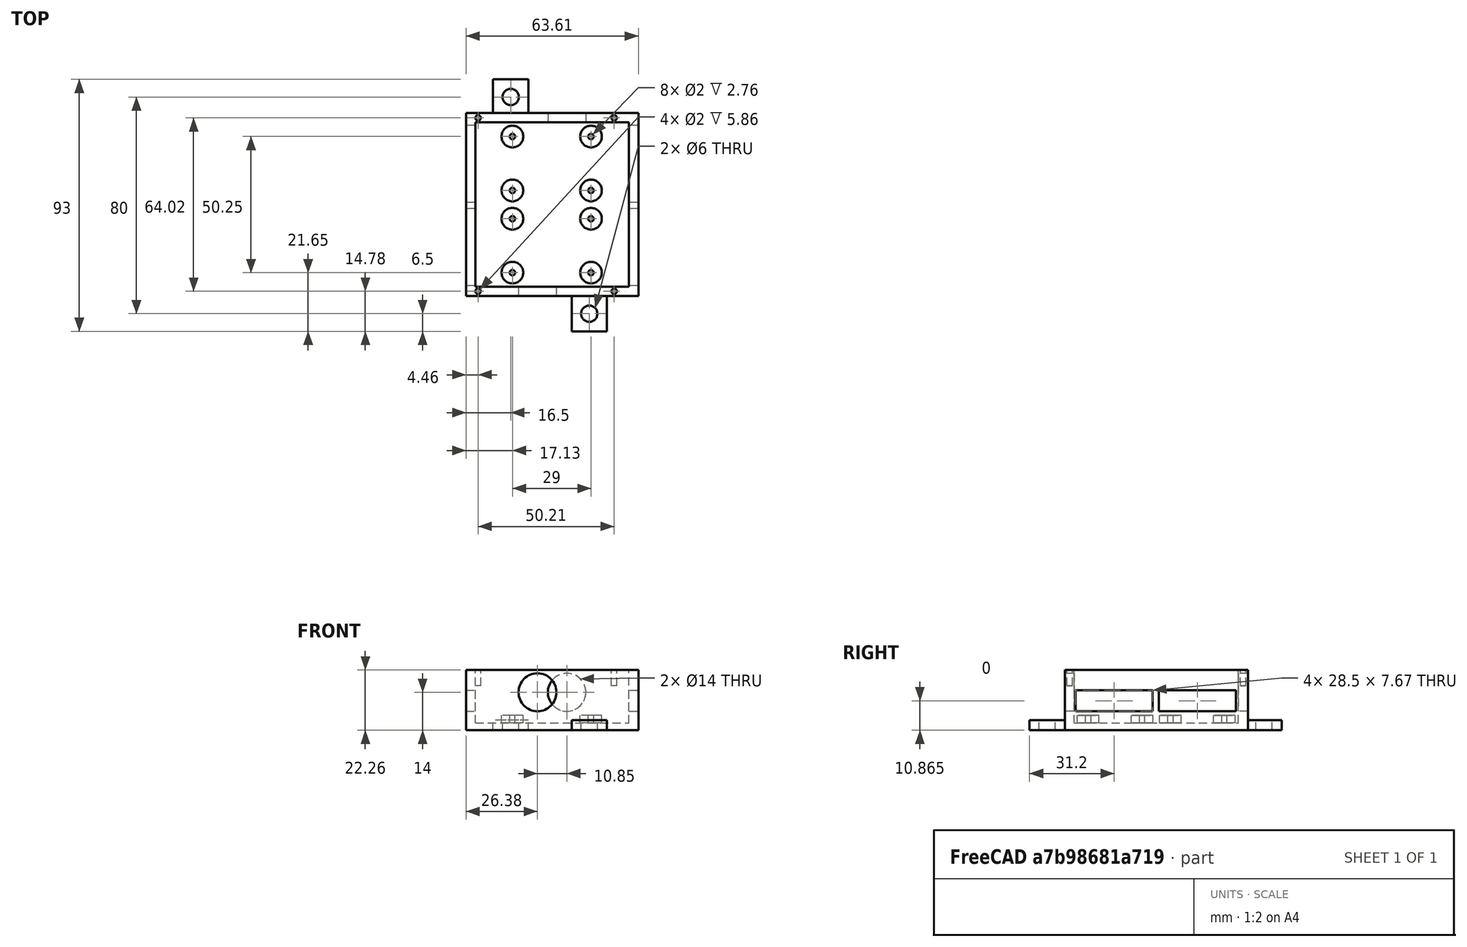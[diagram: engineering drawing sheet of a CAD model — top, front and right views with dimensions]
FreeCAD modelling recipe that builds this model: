
FCSTD DOCUMENT  (FreeCAD 0.15R4671 (Git))
Label: smps_to_dyna_case
License: All rights reserved
LicenseURL: http://en.wikipedia.org/wiki/All_rights_reserved
objects: Part::Cylinder×24, Part::Cut×19, Part::Box×6, Part::MultiFuse×3
note: 52 computed .brp shape members not serialized (recipe doc carries the construction recipe); baked Part::Feature solids carry a one-line shape summary decoded from their .brp

FEATURE [Part::Box] Box  label="Cubo"
  Height = 22.26
  Length = 63.61
  Placement = pos=(0,0,-1) rot=(0,0,1;0rad)
  Width = 67.58
FEATURE [Part::Box] Box001  label="Cubo001"
  Height = 22.6
  Length = 56.67
  Placement = pos=(3.47,3.47,1.67) rot=(0,0,1;0rad)
  Width = 60.64
FEATURE [Part::Cut] Cut
  Base = -> Box
  Tool = -> Box001
FEATURE [Part::Cylinder] Cylinder  label="Cilindro"
  Angle = 360
  Height = 4.43
  Placement = pos=(17.13,8.65,0) rot=(0,0,1;0rad)
  Radius = 1
FEATURE [Part::Cylinder] Cylinder001  label="Cilindro001"
  Angle = 360
  Height = 4.43
  Placement = pos=(17.13,8.65,0) rot=(0,0,1;0rad)
  Radius = 4
FEATURE [Part::Cut] Cut001  label="1"
  Base = -> Cylinder001
  Tool = -> Cylinder
FEATURE [Part::Cylinder] Cylinder002  label="Cilindro002"
  Angle = 360
  Height = 4.43
  Placement = pos=(17.13,8.65,0) rot=(0,0,1;0rad)
  Radius = 1
FEATURE [Part::Cylinder] Cylinder003  label="Cilindro003"
  Angle = 360
  Height = 4.43
  Placement = pos=(17.13,8.65,0) rot=(0,0,1;0rad)
  Radius = 4
FEATURE [Part::Cut] Cut002  label="2"
  Base = -> Cylinder003
  Placement = pos=(29,0,0) rot=(0,0,1;0rad)
  Tool = -> Cylinder002
FEATURE [Part::Cylinder] Cylinder004  label="Cilindro004"
  Angle = 360
  Height = 4.43
  Placement = pos=(17.13,8.65,0) rot=(0,0,1;0rad)
  Radius = 1
FEATURE [Part::Cylinder] Cylinder005  label="Cilindro005"
  Angle = 360
  Height = 4.43
  Placement = pos=(17.13,8.65,0) rot=(0,0,1;0rad)
  Radius = 4
FEATURE [Part::Cut] Cut003  label="3"
  Base = -> Cylinder005
  Placement = pos=(29,19.9,0) rot=(0,0,1;0rad)
  Tool = -> Cylinder004
FEATURE [Part::Cylinder] Cylinder006  label="Cilindro006"
  Angle = 360
  Height = 4.43
  Placement = pos=(17.13,8.65,0) rot=(0,0,1;0rad)
  Radius = 1
FEATURE [Part::Cylinder] Cylinder007  label="Cilindro007"
  Angle = 360
  Height = 4.43
  Placement = pos=(17.13,8.65,0) rot=(0,0,1;0rad)
  Radius = 4
FEATURE [Part::Cut] Cut004  label="8"
  Base = -> Cylinder007
  Placement = pos=(29,30.35,0) rot=(0,0,1;0rad)
  Tool = -> Cylinder006
FEATURE [Part::Cylinder] Cylinder008  label="Cilindro008"
  Angle = 360
  Height = 4.43
  Placement = pos=(17.13,8.65,0) rot=(0,0,1;0rad)
  Radius = 1
FEATURE [Part::Cylinder] Cylinder009  label="Cilindro009"
  Angle = 360
  Height = 4.43
  Placement = pos=(17.13,8.65,0) rot=(0,0,1;0rad)
  Radius = 4
FEATURE [Part::Cut] Cut005  label="7"
  Base = -> Cylinder009
  Placement = pos=(0,19.9,0) rot=(0,0,1;0rad)
  Tool = -> Cylinder008
FEATURE [Part::Cylinder] Cylinder010  label="Cilindro010"
  Angle = 360
  Height = 4.43
  Placement = pos=(17.13,8.65,0) rot=(0,0,1;0rad)
  Radius = 1
FEATURE [Part::Cylinder] Cylinder011  label="Cilindro011"
  Angle = 360
  Height = 4.43
  Placement = pos=(17.13,8.65,0) rot=(0,0,1;0rad)
  Radius = 4
FEATURE [Part::Cut] Cut006  label="6"
  Base = -> Cylinder011
  Placement = pos=(0,30.35,0) rot=(0,0,1;0rad)
  Tool = -> Cylinder010
FEATURE [Part::Cylinder] Cylinder012  label="Cilindro012"
  Angle = 360
  Height = 4.43
  Placement = pos=(17.13,8.65,0) rot=(0,0,1;0rad)
  Radius = 1
FEATURE [Part::Cylinder] Cylinder013  label="Cilindro013"
  Angle = 360
  Height = 4.43
  Placement = pos=(17.13,8.65,0) rot=(0,0,1;0rad)
  Radius = 4
FEATURE [Part::Cut] Cut007  label="5"
  Base = -> Cylinder013
  Placement = pos=(0,50.25,0) rot=(0,0,1;0rad)
  Tool = -> Cylinder012
FEATURE [Part::Cylinder] Cylinder014  label="Cilindro014"
  Angle = 360
  Height = 4.43
  Placement = pos=(17.13,8.65,0) rot=(0,0,1;0rad)
  Radius = 1
FEATURE [Part::Cylinder] Cylinder015  label="Cilindro015"
  Angle = 360
  Height = 4.43
  Placement = pos=(17.13,8.65,0) rot=(0,0,1;0rad)
  Radius = 4
FEATURE [Part::Cut] Cut008  label="4"
  Base = -> Cylinder015
  Placement = pos=(29,50.25,0) rot=(0,0,1;0rad)
  Tool = -> Cylinder014
FEATURE [Part::Box] Box002  label="Cubo002"
  Height = 7.67
  Length = 100
  Placement = pos=(-18,3.95,6.03) rot=(0,0,1;0rad)
  Width = 28.5
FEATURE [Part::Box] Box003  label="Cubo003"
  Height = 7.67
  Length = 100
  Placement = pos=(-18,34.67,6.03) rot=(0,0,1;0rad)
  Width = 28.5
FEATURE [Part::Cut] Cut009
  Base = -> Cut
  Tool = -> Box002
FEATURE [Part::Cut] Cut010
  Base = -> Cut009
  Tool = -> Box003
FEATURE [Part::Cylinder] Cylinder017  label="Cilindro017"
  Angle = 360
  Height = 30
  Placement = pos=(26.38,19,13) rot=(1,0,0;1.5708rad)
  Radius = 7
FEATURE [Part::Cylinder] Cylinder018  label="Cilindro018"
  Angle = 360
  Height = 30
  Placement = pos=(37.23,80,13) rot=(1,0,0;1.5708rad)
  Radius = 7
FEATURE [Part::Cut] Cut011
  Base = -> Cut010
  Tool = -> Cylinder017
FEATURE [Part::Cut] Cut012
  Base = -> Cut011
  Tool = -> Cylinder018
FEATURE [Part::Cylinder] Cylinder019  label="4001"
  Angle = 360
  Height = 40
  Placement = pos=(4.46,1.78,15.4) rot=(0,0,1;0rad)
  Radius = 1
FEATURE [Part::Cylinder] Cylinder020  label="1001"
  Angle = 360
  Height = 40
  Placement = pos=(54.67,1.78,15.4) rot=(0,0,1;0rad)
  Radius = 1
FEATURE [Part::Cylinder] Cylinder021  label="3001"
  Angle = 360
  Height = 40
  Placement = pos=(4.46,65.8,15.4) rot=(0,0,1;0rad)
  Radius = 1
FEATURE [Part::Cylinder] Cylinder022  label="2001"
  Angle = 360
  Height = 40
  Placement = pos=(54.67,65.8,15.4) rot=(0,0,1;0rad)
  Radius = 1
FEATURE [Part::MultiFuse] Fusion
  Shapes = -> [Cut004,Cut007,Cut006,Cut005,Cut008,Cut001,Cut002,Cut003]
FEATURE [Part::Cut] Cut013
  Base = -> Cut012
  Tool = -> Cylinder020
FEATURE [Part::Cut] Cut014
  Base = -> Cut013
  Tool = -> Cylinder022
FEATURE [Part::Cut] Cut015
  Base = -> Cut014
  Tool = -> Cylinder021
FEATURE [Part::Cut] Cut016
  Base = -> Cut015
  Tool = -> Cylinder019
FEATURE [Part::Box] Box005  label="Cubo004"
  Height = 3.7
  Length = 13
  Placement = pos=(0,0,-1) rot=(0,0,1;0rad)
  Width = 13
FEATURE [Part::Cylinder] Cylinder023  label="Cilindro019"
  Angle = 360
  Height = 10
  Placement = pos=(6.5,6.5,-3) rot=(0,0,1;0rad)
  Radius = 3
FEATURE [Part::Cut] Cut022
  Base = -> Box005
  Placement = pos=(39,-13,0) rot=(0,0,1;0rad)
  Tool = -> Cylinder023
FEATURE [Part::Box] Box006  label="Cubo005"
  Height = 3.7
  Length = 13
  Placement = pos=(0,0,-1) rot=(0,0,1;0rad)
  Width = 13
FEATURE [Part::Cylinder] Cylinder024  label="Cilindro020"
  Angle = 360
  Height = 10
  Placement = pos=(6.5,6.5,-3) rot=(0,0,1;0rad)
  Radius = 3
FEATURE [Part::Cut] Cut023
  Base = -> Box006
  Placement = pos=(10,67,0) rot=(0,0,1;0rad)
  Tool = -> Cylinder024
FEATURE [Part::MultiFuse] Fusion001
  Shapes = -> [Cut022,Cut023,Cut016]
FEATURE [Part::MultiFuse] Fusion002  label="case"
  Shapes = -> [Fusion,Fusion001]
